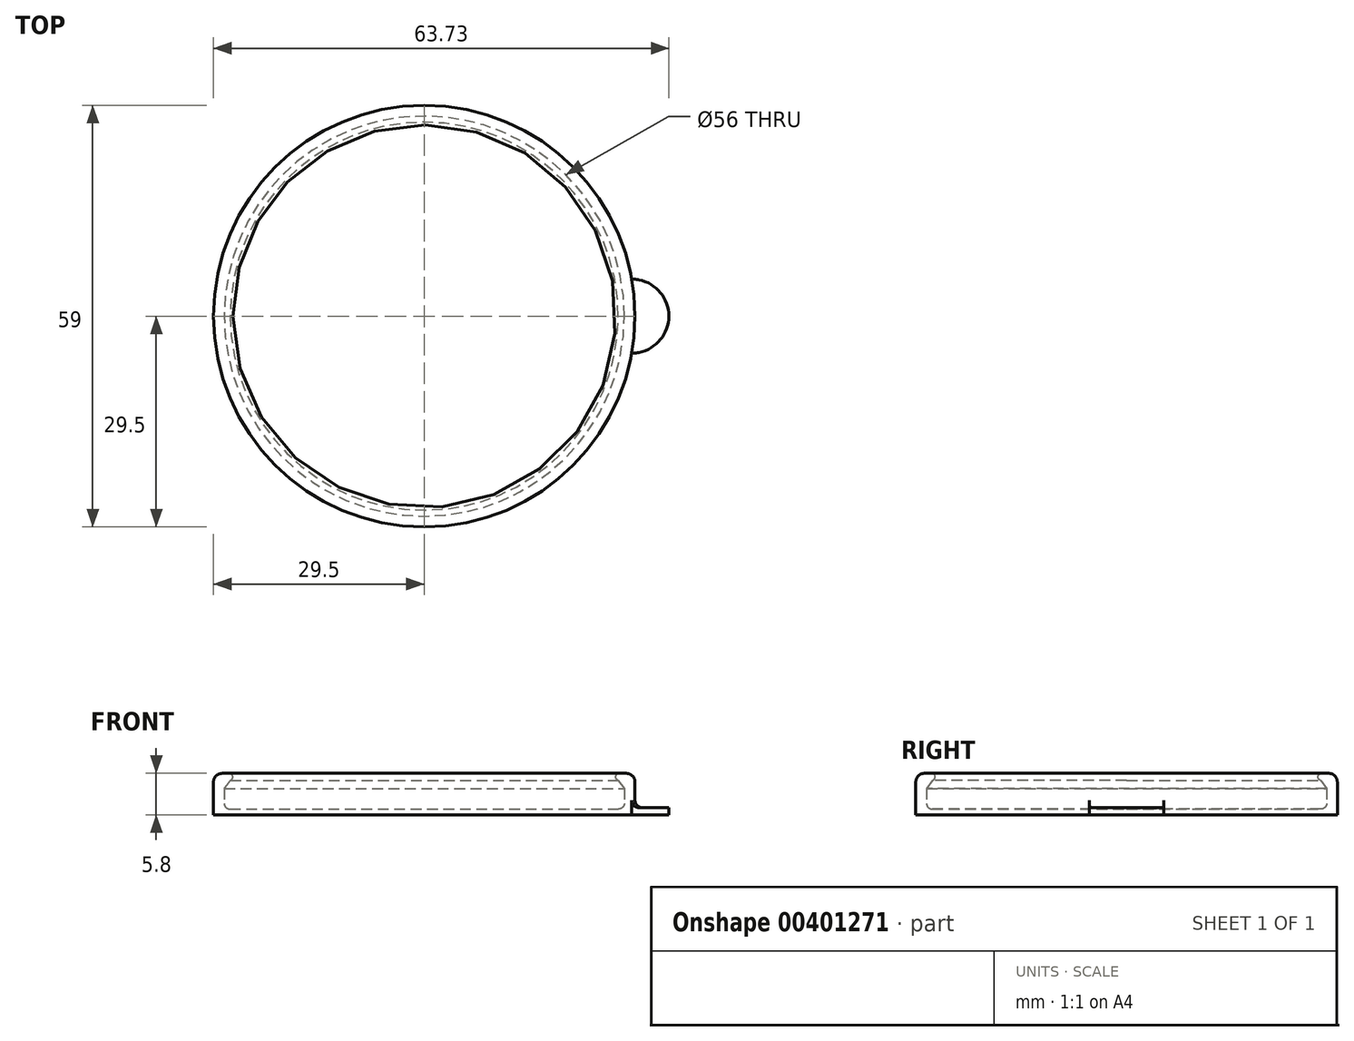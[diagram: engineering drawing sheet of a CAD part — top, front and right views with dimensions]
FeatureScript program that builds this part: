
annotation { "Feature Type Name" : "Feature", "Feature Type Description" : "" }
export const myFeature = defineFeature(function(context is Context, id is Id, definition is map)
    precondition{}
    {
        {
            var Q0;
            Q0=qCreatedBy(makeId("Front.planeOp"),FACE);
            var sketch = newSketch(context, id + "F0", { "sketchPlane" : qUnion([Q0])});
            skLineSegment(sketch, "E0", {"start": v(0, 0) * mm, "end": v(0, 0.8) * mm});
            skLineSegment(sketch, "E1", {"start": v(0, 0.8) * mm, "end": v(26.8, 0.8) * mm});
            skLineSegment(sketch, "E2", {"start": v(26.8, 5.8) * mm, "end": v(28.3, 5.8) * mm});
            skLineSegment(sketch, "E3", {"start": v(29.5, 4.6) * mm, "end": v(29.5, 0) * mm});
            skLineSegment(sketch, "E4", {"start": v(29.5, 0) * mm, "end": v(0, 0) * mm});
            skLineSegment(sketch, "E5", {"start": v(26.8, 5.8) * mm, "end": v(26.8, 4.8) * mm});
            skLineSegment(sketch, "E6", {"start": v(28, 4.8) * mm, "end": v(28, 1.6) * mm});
            skLineSegment(sketch, "E7", {"start": v(27.2, 0.8) * mm, "end": v(26.8, 0.8) * mm});
            skPoint(sketch, "E8.visualSharp", {"position": v(28, 5.3) * mm});
            skPoint(sketch, "E9.visualSharp", {"position": v(28, 0.8) * mm});
            skArc(sketch, "E9.filletArc", {"start": v(27.2, 0.8) * mm, "mid": v(27.77, 1.03) * mm, "end": v(28, 1.6) * mm});
            skPoint(sketch, "E10.visualSharp", {"position": v(29.5, 5.8) * mm});
            skArc(sketch, "E10.filletArc", {"start": v(29.5, 4.6) * mm, "mid": v(29.15, 5.45) * mm, "end": v(28.3, 5.8) * mm});
            skPoint(sketch, "E11.visualSharp", {"position": v(29.5, 0) * mm});
            skLineSegment(sketch, "E12", {"start": v(26.8, 4.8) * mm, "end": v(28, 4.8) * mm});
            skSolve(sketch);
        }
        {
            var Q0;
            Q0 = qSketchRegion(id + "F0", true);
            var Q1;
            Q1=sQuery(id+"F0.wireOp",EDGE,"E0");
            revolve(context, id + "F1", {"entities" : qUnion([Q0]), "axis" : qUnion([Q1]), "revolveType" : RevolveType.FULL});
        }
        {
            var Q0;
            Q0=makeQuery(id+"F1.opRevolve","SWEPT_EDGE",EDGE,{"disambiguationData":[OSD([sQuery(id+"F0.wireOp",EDGE,"E2"),sQuery(id+"F0.wireOp",EDGE,"E5")])]});
            var Q1;
            Q1=makeQuery(id+"F1.opRevolve","SWEPT_EDGE",EDGE,{"disambiguationData":[OSD([sQuery(id+"F0.wireOp",EDGE,"E5"),sQuery(id+"F0.wireOp",EDGE,"caB6Z0El-ZOFv-nd8C-T2XF-bNLPoTO0AisI")])]});
            fillet(context, id + "F2", {"entities" : qUnion([Q0, Q1]), "radius" : .5 * mm, "tangentPropagation" : true, "allowEdgeOverflow" : false});
        }
        {
            var Q0;
            Q0=qCreatedBy(makeId("Top.planeOp"),FACE);
            var sketch = newSketch(context, id + "F3", { "sketchPlane" : qUnion([Q0])});
            skLineSegment(sketch, "E13", {"start": v(29.04, 5.19) * mm, "end": v(29.04, -5.19) * mm});
            skPoint(sketch, "E14", {"position": v(29.04, 0) * mm});
            skArc(sketch, "E15", {"start": v(29.04, -5.19) * mm, "mid": v(34.23, 0) * mm, "end": v(29.04, 5.19) * mm});
            skSolve(sketch);
        }
        {
            var Q0;
            Q0 = qSketchRegion(id + "F3", true);
            extrude(context, id + "F4", {"entities" : qUnion([Q0]), "operationType" : NewBodyOperationType.ADD, "depth" : 1 * mm});
        }
        {
            var Q0;
            Q0=makeQuery(id+"F4.boolean.opBoolean","INTERSECT",EDGE,{"derivedFrom":[makeQuery(id+"F1.opRevolve","SWEPT_FACE",FACE,{"disambiguationData":[OSD([sQuery(id+"F0.wireOp",EDGE,"E3")])]}),makeQuery(id+"F4.opExtrude","CAP_FACE",FACE,{"disambiguationData":[OSD([sQuery(id+"F3.wireOp",EDGE,"E13"),sQuery(id+"F3.wireOp",EDGE,"E15")])],"isStart":false})]});
            var Q1;
            {var subQ0=sQuery(id+"F3.wireOp",EDGE,"E15");var subQ1=sQuery(id+"F3.wireOp",EDGE,"E13");Q1=makeQuery(id+"F4.opExtrude","SWEPT_EDGE",EDGE,{"disambiguationData":[OSD([subQ1,subQ0]),TDD([makeQuery(id+"F3.imprint","INTERSECT",VERTEX,{"disambiguationData":[OD(0.0)],"derivedFrom":[subQ1,subQ0]})])]});}
            var Q2;
            {var subQ0=sQuery(id+"F3.wireOp",EDGE,"E15");var subQ1=sQuery(id+"F3.wireOp",EDGE,"E13");Q2=makeQuery(id+"F4.opExtrude","SWEPT_EDGE",EDGE,{"disambiguationData":[OSD([subQ1,subQ0]),TDD([makeQuery(id+"F3.imprint","INTERSECT",VERTEX,{"disambiguationData":[OD(1.0)],"derivedFrom":[subQ1,subQ0]})])]});}
            fillet(context, id + "F5", {"entities" : qUnion([Q0, Q1, Q2]), "radius" : 1 * mm, "tangentPropagation" : true, "allowEdgeOverflow" : false});
        }
        {
            var Q0;
            Q0=makeQuery(id+"F1.opRevolve","SWEPT_EDGE",EDGE,{"disambiguationData":[OSD([sQuery(id+"F0.wireOp",EDGE,"E6"),sQuery(id+"F0.wireOp",EDGE,"E12")])]});
            chamfer(context, id + "F6", {"entities" : qUnion([Q0]), "width" : 1.2 * mm, "tangentPropagation" : true});
        }
    });
